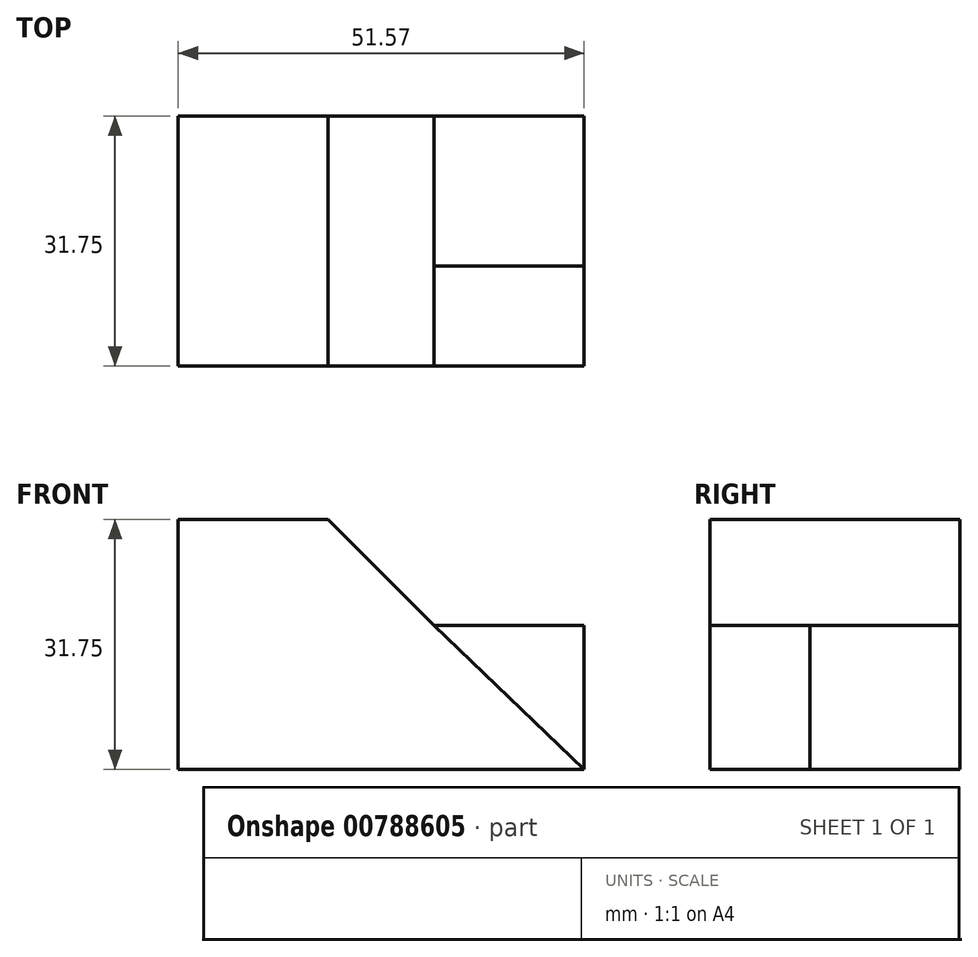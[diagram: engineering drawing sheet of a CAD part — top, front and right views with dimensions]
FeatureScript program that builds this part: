
annotation { "Feature Type Name" : "Feature", "Feature Type Description" : "" }
export const myFeature = defineFeature(function(context is Context, id is Id, definition is map)
    precondition{}
    {
        {
            var Q0;
            Q0=qCreatedBy(makeId("Front.planeOp"),FACE);
            var sketch = newSketch(context, id + "F0", { "sketchPlane" : qUnion([Q0])});
            skLineSegment(sketch, "E0", {"start": v(0, 0) * mm, "end": v(50.8, 0) * mm});
            skLineSegment(sketch, "E1", {"start": v(50.8, 0) * mm, "end": v(50.8, 31.75) * mm});
            skLineSegment(sketch, "E2", {"start": v(0, 0) * mm, "end": v(0, 31.75) * mm});
            skLineSegment(sketch, "E3", {"start": v(0, 31.75) * mm, "end": v(50.8, 31.75) * mm});
            skSolve(sketch);
        }
        {
            var Q0;
            Q0=makeQuery(id+"F0.imprint","IMPRINT",FACE,{"disambiguationData":[TD([[makeQuery(id+"F0.imprint","IMPRINT",EDGE,{"derivedFrom":sQuery(id+"F0.wireOp",EDGE,"E0")}),1.0]])]});
            extrude(context, id + "F1", {"entities" : qUnion([Q0]), "depth" : 31.75 * mm, "offsetDistance" : 25.4 * mm});
        }
        {
            var Q0;
            Q0=makeQuery(id+"F1.opExtrude","CAP_FACE",FACE,{"disambiguationData":[OSD([sQuery(id+"F0.wireOp",EDGE,"E0"),sQuery(id+"F0.wireOp",EDGE,"E1"),sQuery(id+"F0.wireOp",EDGE,"E2"),sQuery(id+"F0.wireOp",EDGE,"E3")])],"isStart":false});
            var sketch = newSketch(context, id + "F2", { "sketchPlane" : qUnion([Q0])});
            skLineSegment(sketch, "E4", {"start": v(0, 31.75) * mm, "end": v(19.05, 31.75) * mm});
            skLineSegment(sketch, "E5", {"start": v(19.05, 31.75) * mm, "end": v(50.8, 0) * mm});
            skSolve(sketch);
        }
        {
            var Q0;
            {var subQ0=sQuery(id+"F2.wireOp",EDGE,"E5");Q0=makeQuery(id+"F2.imprint","IMPRINT",FACE,{"disambiguationData":[TD([[makeQuery(id+"F2.imprint","IMPRINT",EDGE,{"derivedFrom":subQ0}),1.0]])]});}
            extrude(context, id + "F3", {"entities" : qUnion([Q0]), "operationType" : NewBodyOperationType.REMOVE, "oppositeDirection" : true, "depth" : 31.75 * mm, "offsetDistance" : 25.4 * mm});
        }
        {
            var Q0;
            Q0=makeQuery(id+"F1.opExtrude","CAP_FACE",FACE,{"disambiguationData":[OSD([sQuery(id+"F0.wireOp",EDGE,"E0"),sQuery(id+"F0.wireOp",EDGE,"E1"),sQuery(id+"F0.wireOp",EDGE,"E2"),sQuery(id+"F0.wireOp",EDGE,"E3")])],"isStart":false});
            var sketch = newSketch(context, id + "F4", { "sketchPlane" : qUnion([Q0])});
            skLineSegment(sketch, "E6", {"start": v(19.05, 31.75) * mm, "end": v(32.52, 18.28) * mm});
            skLineSegment(sketch, "E7", {"start": v(32.52, 18.28) * mm, "end": v(51.57, 18.28) * mm});
            skLineSegment(sketch, "E8", {"start": v(51.57, 18.28) * mm, "end": v(51.57, 0) * mm});
            skLineSegment(sketch, "E9", {"start": v(49.6, 0) * mm, "end": v(51.57, 0) * mm});
            skSolve(sketch);
        }
        {
            var Q0;
            {var subQ0=sQuery(id+"F4.wireOp",EDGE,"E7");Q0=makeQuery(id+"F4.imprint","IMPRINT",FACE,{"disambiguationData":[TD([[makeQuery(id+"F4.imprint","IMPRINT",EDGE,{"derivedFrom":subQ0}),-1.0]])]});}
            extrude(context, id + "F5", {"entities" : qUnion([Q0]), "operationType" : NewBodyOperationType.ADD, "oppositeDirection" : true, "depth" : 31.75 * mm, "offsetDistance" : 25.4 * mm});
        }
        {
            var Q0;
            Q0=makeQuery(id+"F5.boolean.opBoolean","MERGE",FACE,{"derivedFrom":[makeQuery(id+"F1.opExtrude","CAP_FACE",FACE,{"disambiguationData":[OSD([sQuery(id+"F0.wireOp",EDGE,"E0"),sQuery(id+"F0.wireOp",EDGE,"E1"),sQuery(id+"F0.wireOp",EDGE,"E2"),sQuery(id+"F0.wireOp",EDGE,"E3")])],"isStart":false}),makeQuery(id+"F5.opExtrude","CAP_FACE",FACE,{"disambiguationData":[OSD([sQuery(id+"F2.wireOp",EDGE,"E5"),sQuery(id+"F4.wireOp",EDGE,"E7"),sQuery(id+"F4.wireOp",EDGE,"E8"),sQuery(id+"F4.wireOp",EDGE,"E9")])],"isStart":true})]});
            var sketch = newSketch(context, id + "F6", { "sketchPlane" : qUnion([Q0])});
            skLineSegment(sketch, "E10", {"start": v(32.52, 18.28) * mm, "end": v(51.57, 0) * mm});
            skSolve(sketch);
        }
        {
            var Q0;
            Q0=makeQuery(id+"F6.imprint","IMPRINT",FACE,{"disambiguationData":[TD([[makeQuery(id+"F6.imprint","IMPRINT",EDGE,{"derivedFrom":sQuery(id+"F6.wireOp",EDGE,"E10")}),1.0]])]});
            extrude(context, id + "F7", {"entities" : qUnion([Q0]), "operationType" : NewBodyOperationType.REMOVE, "oppositeDirection" : true, "depth" : 12.7 * mm, "offsetDistance" : 25.4 * mm});
        }
    });
